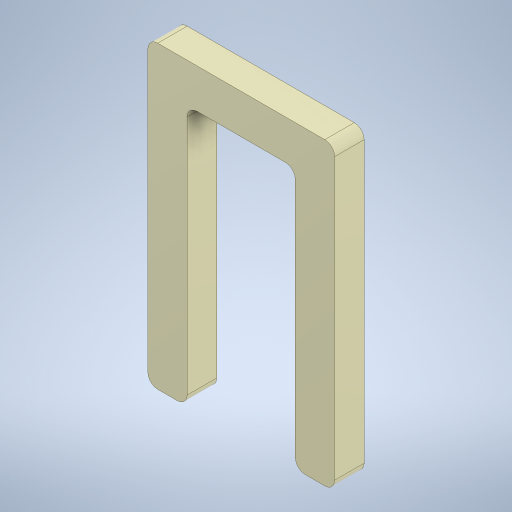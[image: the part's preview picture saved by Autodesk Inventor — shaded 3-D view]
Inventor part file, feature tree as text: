
AUTODESK INVENTOR PART (.ipt)
format: ipt  version: 2024.3 (Build 283343000, 343)  size: 243,200 bytes
history: native  units: mm
features: other x1, extrude x1, fillet x1, sketch x1
ambient origin geometry x8: Origin, YZ Plane, XZ Plane, XY Plane, X Axis, Y Axis, Z Axis, Center Point
bodies: Body1 (feature_tree)
feature tree (4):
  other  "ソリッド1"
  extrude  "押し出し1"  Depth=305.0mm
  fillet  "フィレット1"  Radius=190.0mm
  sketch  "スケッチ1"
